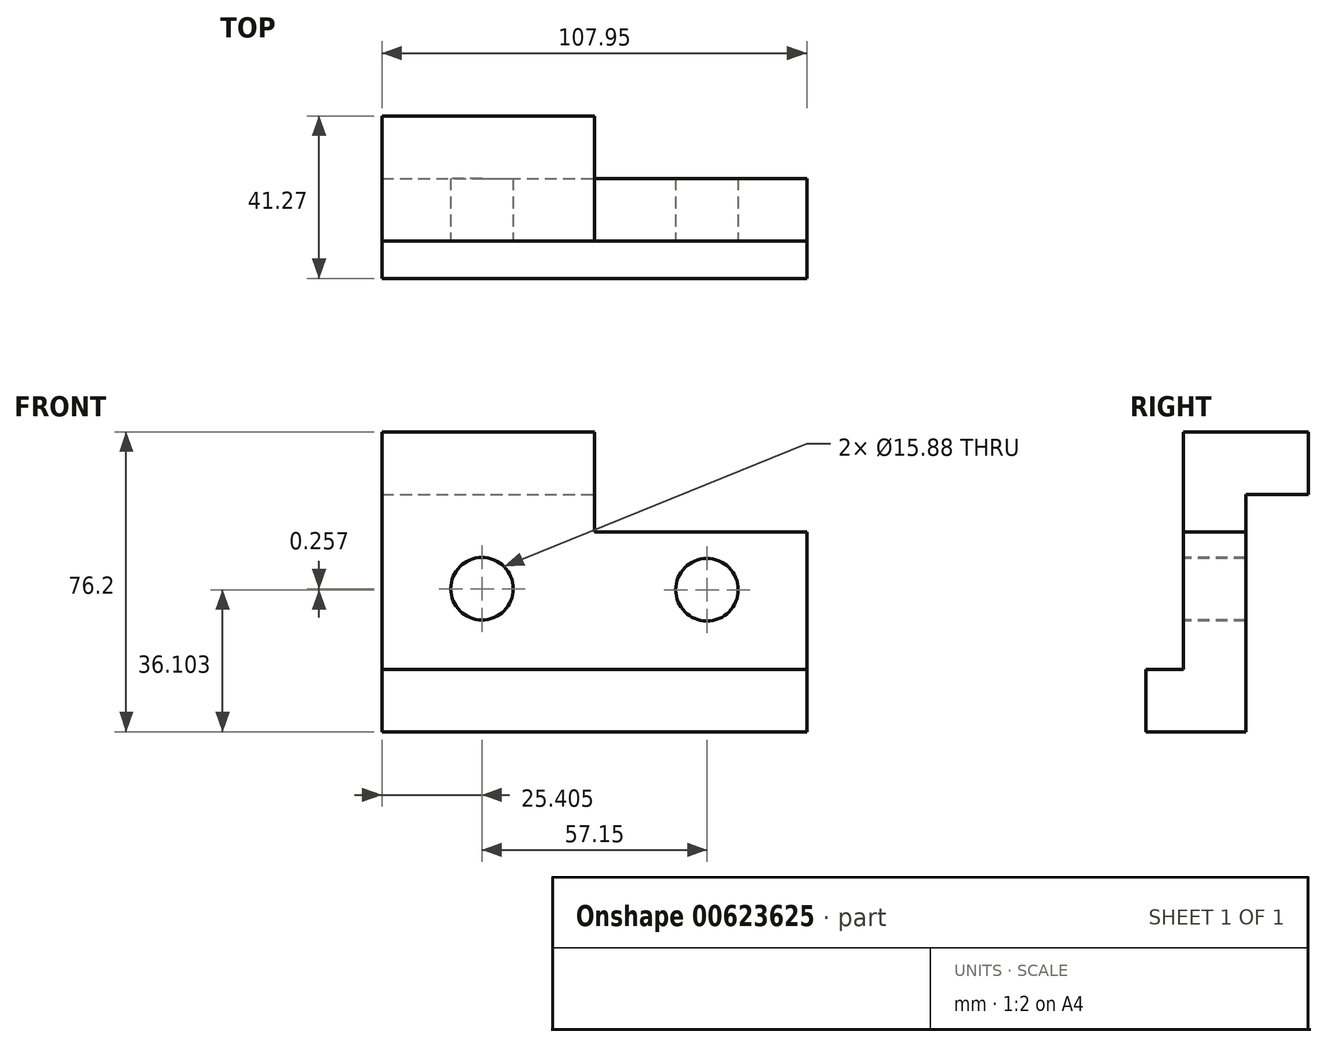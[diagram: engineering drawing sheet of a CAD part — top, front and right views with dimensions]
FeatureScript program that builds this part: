
annotation { "Feature Type Name" : "Feature", "Feature Type Description" : "" }
export const myFeature = defineFeature(function(context is Context, id is Id, definition is map)
    precondition{}
    {
        {
            var Q0;
            Q0=qCreatedBy(makeId("Front.planeOp"),FACE);
            var sketch = newSketch(context, id + "F0", { "sketchPlane" : qUnion([Q0])});
            skLineSegment(sketch, "E0.bottom", {"start": v(-74.3, 29.94) * mm, "end": v(33.64, 29.94) * mm});
            skLineSegment(sketch, "E0.top", {"start": v(-74.3, -46.26) * mm, "end": v(33.64, -46.26) * mm});
            skLineSegment(sketch, "E0.left", {"start": v(-74.3, 29.94) * mm, "end": v(-74.3, -46.26) * mm});
            skLineSegment(sketch, "E0.right", {"start": v(33.64, 29.94) * mm, "end": v(33.64, -46.26) * mm});
            skSolve(sketch);
        }
        {
            var Q0;
            Q0=makeQuery(id+"F0.imprint","IMPRINT",FACE,{"disambiguationData":[TD([[makeQuery(id+"F0.imprint","IMPRINT",EDGE,{"derivedFrom":sQuery(id+"F0.wireOp",EDGE,"E0.bottom")}),-1.0]])]});
            extrude(context, id + "F1", {"entities" : qUnion([Q0]), "depth" : 41.27 * mm, "offsetDistance" : 25.4 * mm});
        }
        {
            var Q0;
            Q0=makeQuery(id+"F1.opExtrude","CAP_FACE",FACE,{"disambiguationData":[OSD([sQuery(id+"F0.wireOp",EDGE,"E0.bottom"),sQuery(id+"F0.wireOp",EDGE,"E0.top"),sQuery(id+"F0.wireOp",EDGE,"E0.left"),sQuery(id+"F0.wireOp",EDGE,"E0.right")])],"isStart":false});
            var sketch = newSketch(context, id + "F2", { "sketchPlane" : qUnion([Q0])});
            skLineSegment(sketch, "E1.bottom", {"start": v(-74.3, 29.94) * mm, "end": v(33.64, 29.94) * mm});
            skLineSegment(sketch, "E1.top", {"start": v(-74.3, -30.39) * mm, "end": v(33.64, -30.39) * mm});
            skLineSegment(sketch, "E1.left", {"start": v(-74.3, 29.94) * mm, "end": v(-74.3, -30.39) * mm});
            skLineSegment(sketch, "E1.right", {"start": v(33.64, 29.94) * mm, "end": v(33.64, -30.39) * mm});
            skSolve(sketch);
        }
        {
            var Q0;
            Q0=makeQuery(id+"F2.imprint","IMPRINT",FACE,{"disambiguationData":[TD([[makeQuery(id+"F2.imprint","IMPRINT",EDGE,{"derivedFrom":sQuery(id+"F2.wireOp",EDGE,"E1.bottom")}),-1.0]])]});
            extrude(context, id + "F3", {"entities" : qUnion([Q0]), "operationType" : NewBodyOperationType.REMOVE, "oppositeDirection" : true, "depth" : 9.52 * mm, "offsetDistance" : 25.4 * mm});
        }
        {
            var Q0;
            Q0=makeQuery(id+"F3.boolean.opBoolean","COPY",FACE,{"derivedFrom":makeQuery(id+"F3.opExtrude","CAP_FACE",FACE,{"disambiguationData":[OSD([sQuery(id+"F2.wireOp",EDGE,"E1.bottom"),sQuery(id+"F2.wireOp",EDGE,"E1.top"),sQuery(id+"F2.wireOp",EDGE,"E1.left"),sQuery(id+"F2.wireOp",EDGE,"E1.right")])],"isStart":false})});
            var sketch = newSketch(context, id + "F4", { "sketchPlane" : qUnion([Q0])});
            skLineSegment(sketch, "E2.bottom", {"start": v(33.64, 29.94) * mm, "end": v(-20.33, 29.94) * mm});
            skLineSegment(sketch, "E2.top", {"start": v(33.64, 4.54) * mm, "end": v(-20.33, 4.54) * mm});
            skLineSegment(sketch, "E2.left", {"start": v(33.64, 29.94) * mm, "end": v(33.64, 4.54) * mm});
            skLineSegment(sketch, "E2.right", {"start": v(-20.33, 29.94) * mm, "end": v(-20.33, 4.54) * mm});
            skSolve(sketch);
        }
        {
            var Q0;
            Q0=makeQuery(id+"F4.imprint","IMPRINT",FACE,{"disambiguationData":[TD([[makeQuery(id+"F4.imprint","IMPRINT",EDGE,{"derivedFrom":sQuery(id+"F4.wireOp",EDGE,"E2.bottom")}),-1.0]])]});
            extrude(context, id + "F5", {"entities" : qUnion([Q0]), "operationType" : NewBodyOperationType.REMOVE, "endBound" : BoundingType.THROUGH_ALL, "oppositeDirection" : true, "depth" : 25.4 * mm, "offsetDistance" : 25.4 * mm});
        }
        {
            var Q0;
            Q0=makeQuery(id+"F1.opExtrude","SWEPT_FACE",FACE,{"disambiguationData":[OSD([sQuery(id+"F0.wireOp",EDGE,"E0.right")])]});
            var sketch = newSketch(context, id + "F6", { "sketchPlane" : qUnion([Q0])});
            skLineSegment(sketch, "E3.bottom", {"start": v(0, -46.26) * mm, "end": v(-15.87, -46.26) * mm});
            skLineSegment(sketch, "E3.top", {"start": v(0, 4.54) * mm, "end": v(-15.87, 4.54) * mm});
            skLineSegment(sketch, "E3.left", {"start": v(0, -46.26) * mm, "end": v(0, 4.54) * mm});
            skLineSegment(sketch, "E3.right", {"start": v(-15.87, -46.26) * mm, "end": v(-15.87, 4.54) * mm});
            skSolve(sketch);
        }
        {
            var Q0;
            Q0=makeQuery(id+"F6.imprint","IMPRINT",FACE,{"disambiguationData":[TD([[makeQuery(id+"F6.imprint","IMPRINT",EDGE,{"derivedFrom":sQuery(id+"F6.wireOp",EDGE,"E3.bottom")}),1.0]])]});
            extrude(context, id + "F7", {"entities" : qUnion([Q0]), "operationType" : NewBodyOperationType.REMOVE, "endBound" : BoundingType.THROUGH_ALL, "oppositeDirection" : true, "depth" : 25.4 * mm, "offsetDistance" : 25.4 * mm});
        }
        {
            var Q0;
            Q0=makeQuery(id+"F5.boolean.opBoolean","COPY",FACE,{"derivedFrom":makeQuery(id+"F5.opExtrude","SWEPT_FACE",FACE,{"disambiguationData":[OSD([sQuery(id+"F4.wireOp",EDGE,"E2.right")])]})});
            var sketch = newSketch(context, id + "F8", { "sketchPlane" : qUnion([Q0])});
            skLineSegment(sketch, "E4.bottom", {"start": v(0, 4.54) * mm, "end": v(-15.87, 4.54) * mm});
            skLineSegment(sketch, "E4.top", {"start": v(0, 14.06) * mm, "end": v(-15.88, 14.06) * mm});
            skLineSegment(sketch, "E4.left", {"start": v(0, 4.54) * mm, "end": v(0, 14.06) * mm});
            skLineSegment(sketch, "E4.right", {"start": v(-15.87, 4.54) * mm, "end": v(-15.87, 14.06) * mm});
            skSolve(sketch);
        }
        {
            var Q0;
            Q0=makeQuery(id+"F8.imprint","IMPRINT",FACE,{"disambiguationData":[TD([[makeQuery(id+"F8.imprint","IMPRINT",EDGE,{"derivedFrom":sQuery(id+"F8.wireOp",EDGE,"E4.bottom")}),-1.0]])]});
            extrude(context, id + "F9", {"entities" : qUnion([Q0]), "operationType" : NewBodyOperationType.REMOVE, "endBound" : BoundingType.THROUGH_ALL, "oppositeDirection" : true, "depth" : 25.4 * mm, "offsetDistance" : 25.4 * mm});
        }
        {
            var Q0;
            Q0=makeQuery(id+"F3.boolean.opBoolean","COPY",FACE,{"derivedFrom":makeQuery(id+"F3.opExtrude","CAP_FACE",FACE,{"disambiguationData":[OSD([sQuery(id+"F2.wireOp",EDGE,"E1.bottom"),sQuery(id+"F2.wireOp",EDGE,"E1.top"),sQuery(id+"F2.wireOp",EDGE,"E1.left"),sQuery(id+"F2.wireOp",EDGE,"E1.right")])],"isStart":false})});
            var sketch = newSketch(context, id + "F10", { "sketchPlane" : qUnion([Q0])});
            skCircle(sketch, "E5", {"center": v(8.24, -10.16) * mm, "radius": 7.94 * mm});
            skCircle(sketch, "E6", {"center": v(-48.9, -9.9) * mm, "radius": 7.94 * mm});
            skSolve(sketch);
        }
        {
            var Q0;
            Q0=makeQuery(id+"F10.imprint","IMPRINT",FACE,{"disambiguationData":[TD([[makeQuery(id+"F10.imprint","IMPRINT",EDGE,{"derivedFrom":sQuery(id+"F10.wireOp",EDGE,"E6")}),1.0]])]});
            var Q1;
            Q1=makeQuery(id+"F10.imprint","IMPRINT",FACE,{"disambiguationData":[TD([[makeQuery(id+"F10.imprint","IMPRINT",EDGE,{"derivedFrom":sQuery(id+"F10.wireOp",EDGE,"E5")}),1.0]])]});
            extrude(context, id + "F11", {"entities" : qUnion([Q0, Q1]), "operationType" : NewBodyOperationType.REMOVE, "endBound" : BoundingType.THROUGH_ALL, "oppositeDirection" : true, "depth" : 25.4 * mm, "offsetDistance" : 25.4 * mm});
        }
    });
